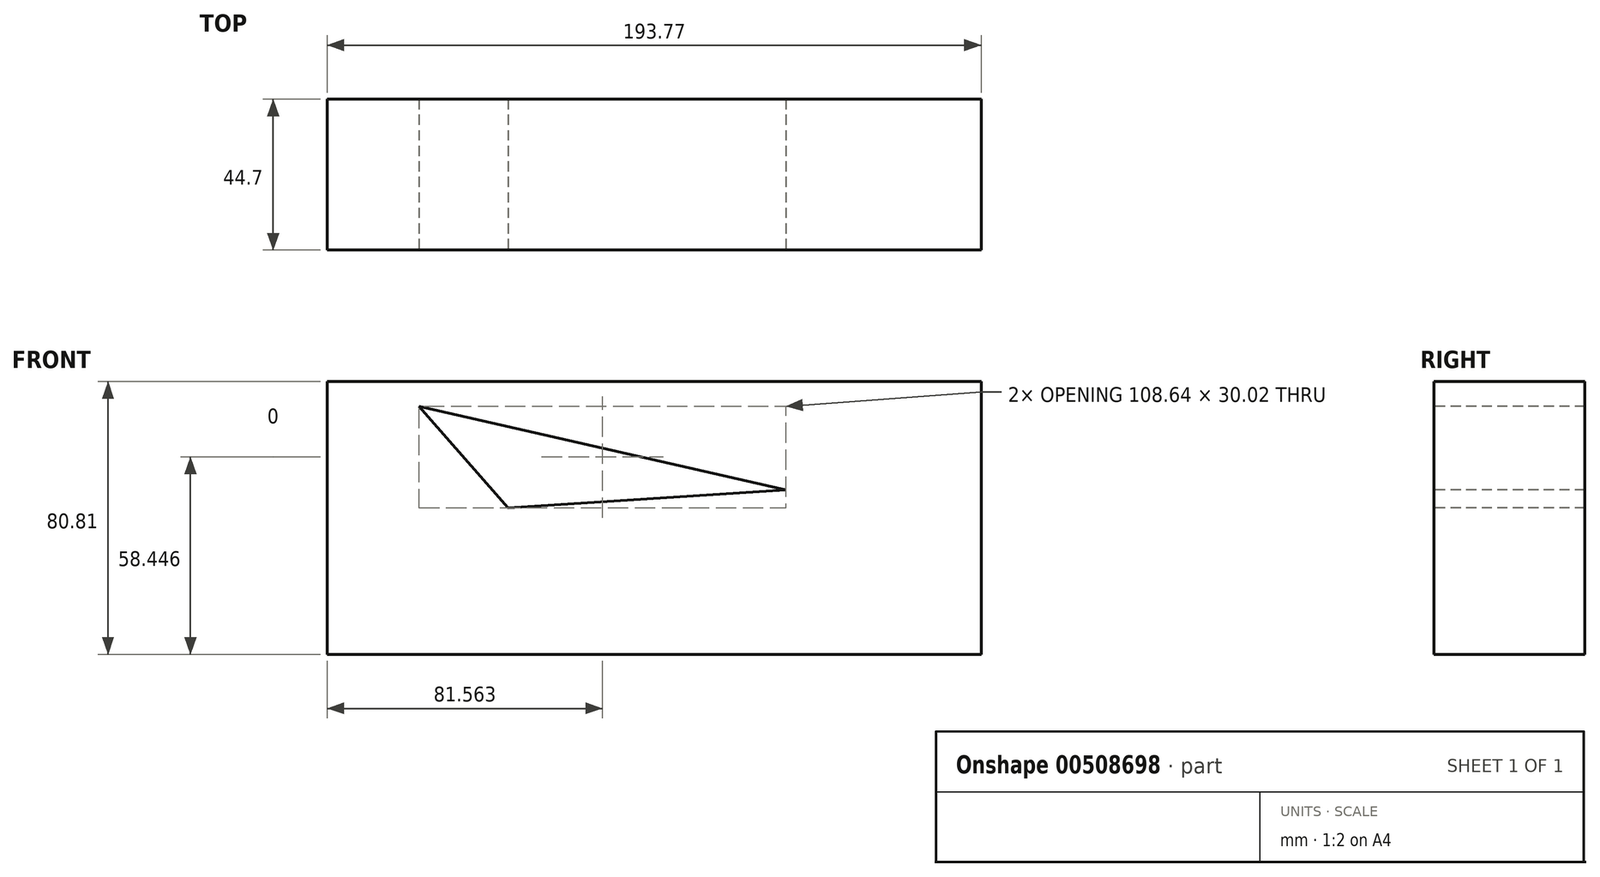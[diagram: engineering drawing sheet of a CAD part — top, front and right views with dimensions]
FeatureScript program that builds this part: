
annotation { "Feature Type Name" : "Feature", "Feature Type Description" : "" }
export const myFeature = defineFeature(function(context is Context, id is Id, definition is map)
    precondition{}
    {
        {
            var Q0;
            Q0=qCreatedBy(makeId("Front.planeOp"),FACE);
            var sketch = newSketch(context, id + "F0", { "sketchPlane" : qUnion([Q0])});
            skLineSegment(sketch, "E0.bottom", {"start": v(-102.42, 44.34) * mm, "end": v(91.35, 44.34) * mm});
            skLineSegment(sketch, "E0.top", {"start": v(-102.42, -36.47) * mm, "end": v(91.35, -36.47) * mm});
            skLineSegment(sketch, "E0.left", {"start": v(-102.42, 44.34) * mm, "end": v(-102.42, -36.47) * mm});
            skLineSegment(sketch, "E0.right", {"start": v(91.35, 44.34) * mm, "end": v(91.35, -36.47) * mm});
            skSolve(sketch);
        }
        {
            var Q0;
            Q0 = qSketchRegion(id + "F0", true);
            extrude(context, id + "F1", {"entities" : qUnion([Q0]), "depth" : 44.7 * mm});
        }
        {
            var Q0;
            Q0=makeQuery(id+"F1.opExtrude","CAP_FACE",FACE,{"disambiguationData":[OSD([sQuery(id+"F0.wireOp",EDGE,"E0.bottom"),sQuery(id+"F0.wireOp",EDGE,"E0.top"),sQuery(id+"F0.wireOp",EDGE,"E0.left"),sQuery(id+"F0.wireOp",EDGE,"E0.right")])],"isStart":false});
            var sketch = newSketch(context, id + "F2", { "sketchPlane" : qUnion([Q0])});
            skLineSegment(sketch, "E1", {"start": v(-75.18, 36.99) * mm, "end": v(-48.87, 6.96) * mm});
            skLineSegment(sketch, "E2", {"start": v(-48.87, 6.96) * mm, "end": v(33.46, 12.23) * mm});
            skLineSegment(sketch, "E3", {"start": v(33.46, 12.23) * mm, "end": v(-75.18, 36.99) * mm});
            skSolve(sketch);
        }
        {
            var Q0;
            Q0=makeQuery(id+"F2.imprint","IMPRINT",FACE,{"disambiguationData":[TD([[makeQuery(id+"F2.imprint","IMPRINT",EDGE,{"derivedFrom":sQuery(id+"F2.wireOp",EDGE,"E1")}),1.0]])]});
            extrude(context, id + "F3", {"entities" : qUnion([Q0]), "operationType" : NewBodyOperationType.REMOVE, "oppositeDirection" : true, "depth" : 55.37 * mm});
        }
    });
